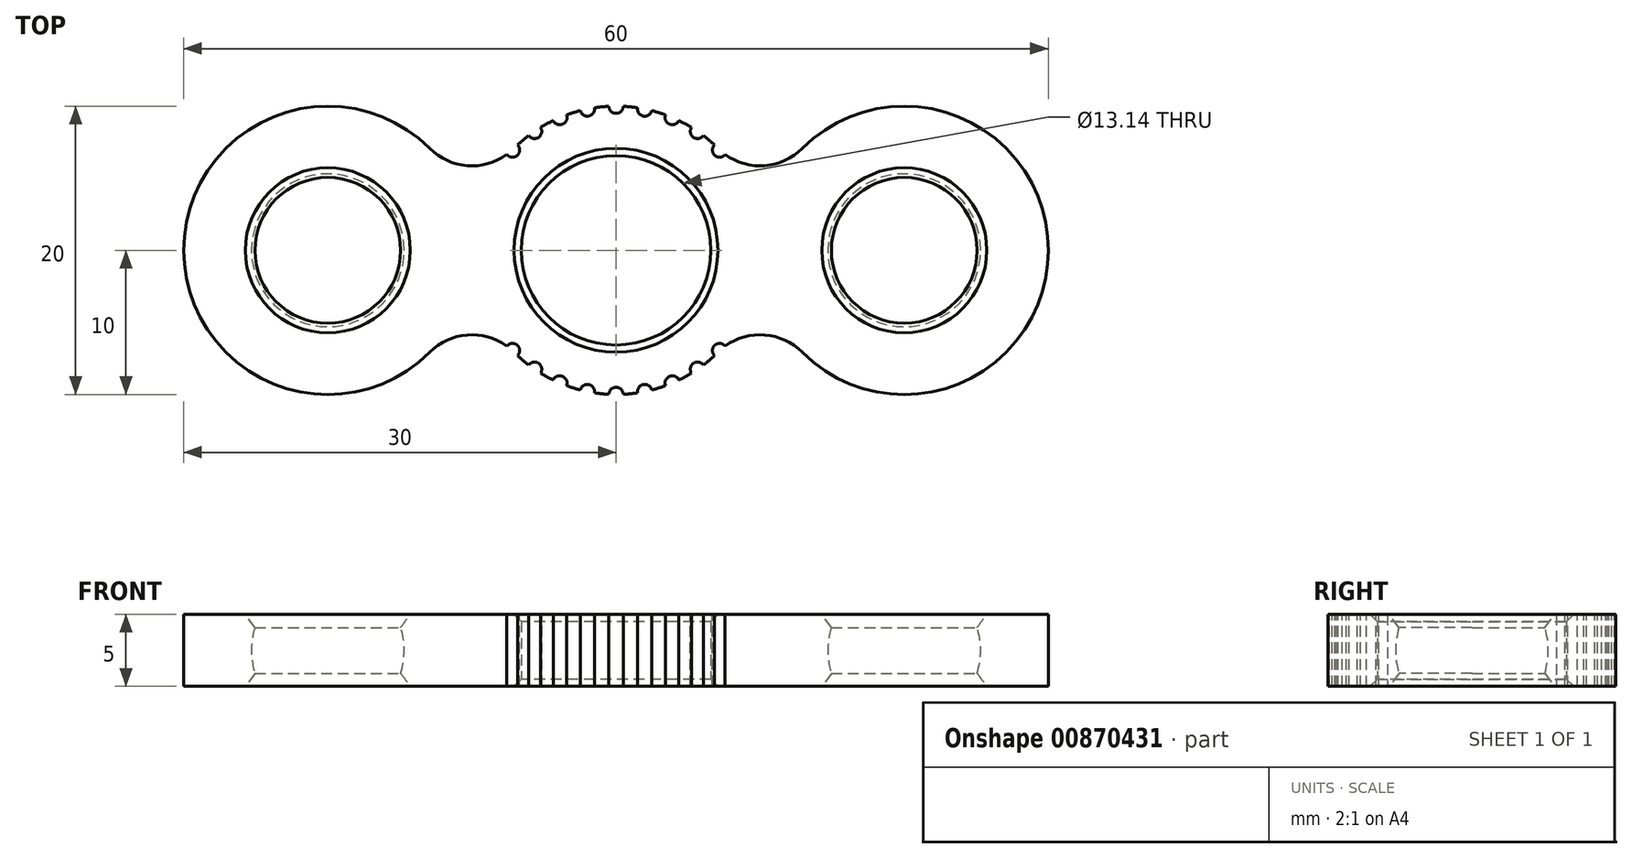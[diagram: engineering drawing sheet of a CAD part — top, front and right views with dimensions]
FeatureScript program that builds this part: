
annotation { "Feature Type Name" : "Feature", "Feature Type Description" : "" }
export const myFeature = defineFeature(function(context is Context, id is Id, definition is map)
    precondition{}
    {
        {
            var Q0;
            Q0=qCreatedBy(makeId("Top.planeOp"),FACE);
            var sketch = newSketch(context, id + "F0", { "sketchPlane" : qUnion([Q0])});
            skArc(sketch, "E0", {"start": v(-7.07, -7.07) * mm, "mid": v(0, -10) * mm, "end": v(7.07, -7.07) * mm});
            skArc(sketch, "E1", {"start": v(12.93, -7.07) * mm, "mid": v(30, 0) * mm, "end": v(12.93, 7.07) * mm});
            skArc(sketch, "E2", {"start": v(-12.93, 7.07) * mm, "mid": v(-30, 0) * mm, "end": v(-12.93, -7.07) * mm});
            skArc(sketch, "E3", {"start": v(7.07, 7.07) * mm, "mid": v(10, 5.86) * mm, "end": v(12.93, 7.07) * mm});
            skArc(sketch, "E4", {"start": v(-12.93, 7.07) * mm, "mid": v(-10, 5.86) * mm, "end": v(-7.07, 7.07) * mm});
            skArc(sketch, "E5.trimOffspring", {"start": v(7.07, 7.07) * mm, "mid": v(0, 10) * mm, "end": v(-7.07, 7.07) * mm});
            skArc(sketch, "E6", {"start": v(-7.07, -7.07) * mm, "mid": v(-10, -5.86) * mm, "end": v(-12.93, -7.07) * mm});
            skArc(sketch, "E7", {"start": v(12.93, -7.07) * mm, "mid": v(10, -5.86) * mm, "end": v(7.07, -7.07) * mm});
            skCircle(sketch, "E8", {"center": v(0, 0) * mm, "radius": 6.57 * mm});
            skSolve(sketch);
        }
        {
            var Q0;
            Q0=makeQuery(id+"F0.imprint","IMPRINT",FACE,{"disambiguationData":[TD([[makeQuery(id+"F0.imprint","IMPRINT",EDGE,{"derivedFrom":sQuery(id+"F0.wireOp",EDGE,"E0")}),1.0]])]});
            extrude(context, id + "F1", {"entities" : qUnion([Q0]), "depth" : 2.5 * mm, "offsetDistance" : 25 * mm});
        }
        {
            var Q0;
            Q0=makeQuery(id+"F1.opExtrude","CAP_FACE",FACE,{"disambiguationData":[OSD([sQuery(id+"F0.wireOp",EDGE,"E0"),sQuery(id+"F0.wireOp",EDGE,"E1"),sQuery(id+"F0.wireOp",EDGE,"E2"),sQuery(id+"F0.wireOp",EDGE,"E3"),sQuery(id+"F0.wireOp",EDGE,"E4"),sQuery(id+"F0.wireOp",EDGE,"E5.trimOffspring"),sQuery(id+"F0.wireOp",EDGE,"E6"),sQuery(id+"F0.wireOp",EDGE,"E7"),sQuery(id+"F0.wireOp",EDGE,"E8")])],"isStart":true});
            extrude(context, id + "F2", {"entities" : qUnion([Q0]), "operationType" : NewBodyOperationType.ADD, "depth" : 2.5 * mm, "offsetDistance" : 25 * mm});
        }
        {
            var Q0;
            Q0=qCreatedBy(makeId("Front.planeOp"),FACE);
            var sketch = newSketch(context, id + "F3", { "sketchPlane" : qUnion([Q0])});
            skArc(sketch, "E9", {"start": v(-20, 5.3) * mm, "mid": v(-25.3, 0) * mm, "end": v(-20, -5.3) * mm});
            skLineSegment(sketch, "E10", {"start": v(-20, 5.3) * mm, "end": v(-20, -5.3) * mm});
            skSolve(sketch);
        }
        {
            var Q0;
            Q0=qSketchRegion(id+"F3",true);
            var Q1;
            Q1=sQuery(id+"F3.wireOp",EDGE,"E10");
            revolve(context, id + "F4", {"operationType" : NewBodyOperationType.REMOVE, "entities" : qUnion([Q0]), "axis" : qUnion([Q1]), "revolveType" : RevolveType.FULL, "oppositeDirection" : true, "surfaceOperationType" : NewSurfaceOperationType.NEW});
        }
        {
            var Q0;
            Q0=qCreatedBy(makeId("Front.planeOp"),FACE);
            var sketch = newSketch(context, id + "F5", { "sketchPlane" : qUnion([Q0])});
            skArc(sketch, "E11", {"start": v(20, -5.3) * mm, "mid": v(25.3, 0) * mm, "end": v(20, 5.3) * mm});
            skLineSegment(sketch, "E12", {"start": v(20, 5.3) * mm, "end": v(20, -5.3) * mm});
            skPoint(sketch, "E13.orphan", {"position": v(20, 9.13) * mm});
            skSolve(sketch);
        }
        {
            var Q0;
            Q0=makeQuery(id+"F5.imprint","IMPRINT",FACE,{"disambiguationData":[TD([[makeQuery(id+"F5.imprint","IMPRINT",EDGE,{"derivedFrom":sQuery(id+"F5.wireOp",EDGE,"E11")}),1.0]])]});
            var Q1;
            Q1=sQuery(id+"F5.wireOp",EDGE,"E12");
            revolve(context, id + "F6", {"operationType" : NewBodyOperationType.REMOVE, "entities" : qUnion([Q0]), "axis" : qUnion([Q1]), "revolveType" : RevolveType.FULL, "oppositeDirection" : true});
        }
        {
            var Q0;
            {var subQ0=sQuery(id+"F0.wireOp",EDGE,"E8");Q0=makeQuery(id+"F2.boolean.opBoolean","MERGE",FACE,{"derivedFrom":[makeQuery(id+"F1.opExtrude","SWEPT_FACE",FACE,{"disambiguationData":[OSD([subQ0])]}),makeQuery(id+"F2.opExtrude","SWEPT_FACE",FACE,{"disambiguationData":[OSD([subQ0])]})]});}
            chamfer(context, id + "F7", {"entities" : qUnion([Q0]), "width" : 0.5 * mm, "tangentPropagation" : true});
        }
        {
            var Q0;
            Q0=makeQuery(id+"F1.opExtrude","CAP_FACE",FACE,{"disambiguationData":[OSD([sQuery(id+"F0.wireOp",EDGE,"E0"),sQuery(id+"F0.wireOp",EDGE,"E1"),sQuery(id+"F0.wireOp",EDGE,"E2"),sQuery(id+"F0.wireOp",EDGE,"E3"),sQuery(id+"F0.wireOp",EDGE,"E4"),sQuery(id+"F0.wireOp",EDGE,"E5.trimOffspring"),sQuery(id+"F0.wireOp",EDGE,"E6"),sQuery(id+"F0.wireOp",EDGE,"E7"),sQuery(id+"F0.wireOp",EDGE,"E8")])],"isStart":false});
            var sketch = newSketch(context, id + "F8", { "sketchPlane" : qUnion([Q0])});
            skCircle(sketch, "E14", {"center": v(0, 10) * mm, "radius": 0.5 * mm});
            skCircle(sketch, "E15", {"center": v(1.99, 9.8) * mm, "radius": 0.5 * mm});
            skCircle(sketch, "E16", {"center": v(3.9, 9.2) * mm, "radius": 0.5 * mm});
            skCircle(sketch, "E17", {"center": v(5.65, 8.25) * mm, "radius": 0.5 * mm});
            skCircle(sketch, "E18", {"center": v(7.18, 6.96) * mm, "radius": 0.5 * mm});
            skCircle(sketch, "E19.MirrorC", {"center": v(-1.99, 9.8) * mm, "radius": 0.5 * mm});
            skCircle(sketch, "E20.MirrorC", {"center": v(-3.9, 9.2) * mm, "radius": 0.5 * mm});
            skCircle(sketch, "E21.MirrorC", {"center": v(-5.65, 8.25) * mm, "radius": 0.5 * mm});
            skCircle(sketch, "E22.MirrorC", {"center": v(-7.18, 6.96) * mm, "radius": 0.5 * mm});
            skCircle(sketch, "E23.MirrorC", {"center": v(7.18, -6.96) * mm, "radius": 0.5 * mm});
            skCircle(sketch, "E24.MirrorC", {"center": v(-7.18, -6.96) * mm, "radius": 0.5 * mm});
            skCircle(sketch, "E25.MirrorC", {"center": v(5.65, -8.25) * mm, "radius": 0.5 * mm});
            skCircle(sketch, "E26.MirrorC", {"center": v(-5.65, -8.25) * mm, "radius": 0.5 * mm});
            skCircle(sketch, "E27.MirrorC", {"center": v(-3.9, -9.2) * mm, "radius": 0.5 * mm});
            skCircle(sketch, "E28.MirrorC", {"center": v(1.99, -9.8) * mm, "radius": 0.5 * mm});
            skCircle(sketch, "E29.MirrorC", {"center": v(-1.99, -9.8) * mm, "radius": 0.5 * mm});
            skCircle(sketch, "E30.MirrorC", {"center": v(0, -10) * mm, "radius": 0.5 * mm});
            skCircle(sketch, "E31.MirrorC", {"center": v(3.9, -9.2) * mm, "radius": 0.5 * mm});
            skSolve(sketch);
        }
        {
            var Q0;
            Q0=qSketchRegion(id+"F8",true);
            extrude(context, id + "F9", {"entities" : qUnion([Q0]), "operationType" : NewBodyOperationType.REMOVE, "oppositeDirection" : true, "depth" : 25 * mm, "offsetDistance" : 25 * mm});
        }
        {
            var Q0;
            Q0=makeQuery(id+"F6.boolean.opBoolean","INTERSECT",EDGE,{"derivedFrom":[makeQuery(id+"F1.opExtrude","CAP_FACE",FACE,{"disambiguationData":[OSD([sQuery(id+"F0.wireOp",EDGE,"E0"),sQuery(id+"F0.wireOp",EDGE,"E1"),sQuery(id+"F0.wireOp",EDGE,"E2"),sQuery(id+"F0.wireOp",EDGE,"E3"),sQuery(id+"F0.wireOp",EDGE,"E4"),sQuery(id+"F0.wireOp",EDGE,"E5.trimOffspring"),sQuery(id+"F0.wireOp",EDGE,"E6"),sQuery(id+"F0.wireOp",EDGE,"E7"),sQuery(id+"F0.wireOp",EDGE,"E8")])],"isStart":false}),makeQuery(id+"F6.opRevolve","SWEPT_FACE",FACE,{"disambiguationData":[OSD([sQuery(id+"F5.wireOp",EDGE,"E11")])]})]});
            var Q1;
            Q1=makeQuery(id+"F6.boolean.opBoolean","INTERSECT",EDGE,{"derivedFrom":[makeQuery(id+"F2.opExtrude","CAP_FACE",FACE,{"disambiguationData":[OSD([sQuery(id+"F0.wireOp",EDGE,"E0"),sQuery(id+"F0.wireOp",EDGE,"E1"),sQuery(id+"F0.wireOp",EDGE,"E2"),sQuery(id+"F0.wireOp",EDGE,"E3"),sQuery(id+"F0.wireOp",EDGE,"E4"),sQuery(id+"F0.wireOp",EDGE,"E5.trimOffspring"),sQuery(id+"F0.wireOp",EDGE,"E6"),sQuery(id+"F0.wireOp",EDGE,"E7"),sQuery(id+"F0.wireOp",EDGE,"E8")])],"isStart":false}),makeQuery(id+"F6.opRevolve","SWEPT_FACE",FACE,{"disambiguationData":[OSD([sQuery(id+"F5.wireOp",EDGE,"E11")])]})]});
            var Q2;
            Q2=makeQuery(id+"F4.boolean.opBoolean","INTERSECT",EDGE,{"derivedFrom":[makeQuery(id+"F1.opExtrude","CAP_FACE",FACE,{"disambiguationData":[OSD([sQuery(id+"F0.wireOp",EDGE,"E0"),sQuery(id+"F0.wireOp",EDGE,"E1"),sQuery(id+"F0.wireOp",EDGE,"E2"),sQuery(id+"F0.wireOp",EDGE,"E3"),sQuery(id+"F0.wireOp",EDGE,"E4"),sQuery(id+"F0.wireOp",EDGE,"E5.trimOffspring"),sQuery(id+"F0.wireOp",EDGE,"E6"),sQuery(id+"F0.wireOp",EDGE,"E7"),sQuery(id+"F0.wireOp",EDGE,"E8")])],"isStart":false}),makeQuery(id+"F4.opRevolve","SWEPT_FACE",FACE,{"disambiguationData":[OSD([sQuery(id+"F3.wireOp",EDGE,"E9")])]})]});
            var Q3;
            Q3=makeQuery(id+"F4.boolean.opBoolean","INTERSECT",EDGE,{"derivedFrom":[makeQuery(id+"F2.opExtrude","CAP_FACE",FACE,{"disambiguationData":[OSD([sQuery(id+"F0.wireOp",EDGE,"E0"),sQuery(id+"F0.wireOp",EDGE,"E1"),sQuery(id+"F0.wireOp",EDGE,"E2"),sQuery(id+"F0.wireOp",EDGE,"E3"),sQuery(id+"F0.wireOp",EDGE,"E4"),sQuery(id+"F0.wireOp",EDGE,"E5.trimOffspring"),sQuery(id+"F0.wireOp",EDGE,"E6"),sQuery(id+"F0.wireOp",EDGE,"E7"),sQuery(id+"F0.wireOp",EDGE,"E8")])],"isStart":false}),makeQuery(id+"F4.opRevolve","SWEPT_FACE",FACE,{"disambiguationData":[OSD([sQuery(id+"F3.wireOp",EDGE,"E9")])]})]});
            chamfer(context, id + "F10", {"entities" : qUnion([Q0, Q1, Q2, Q3]), "width" : 0.7 * mm, "tangentPropagation" : true});
        }
    });
